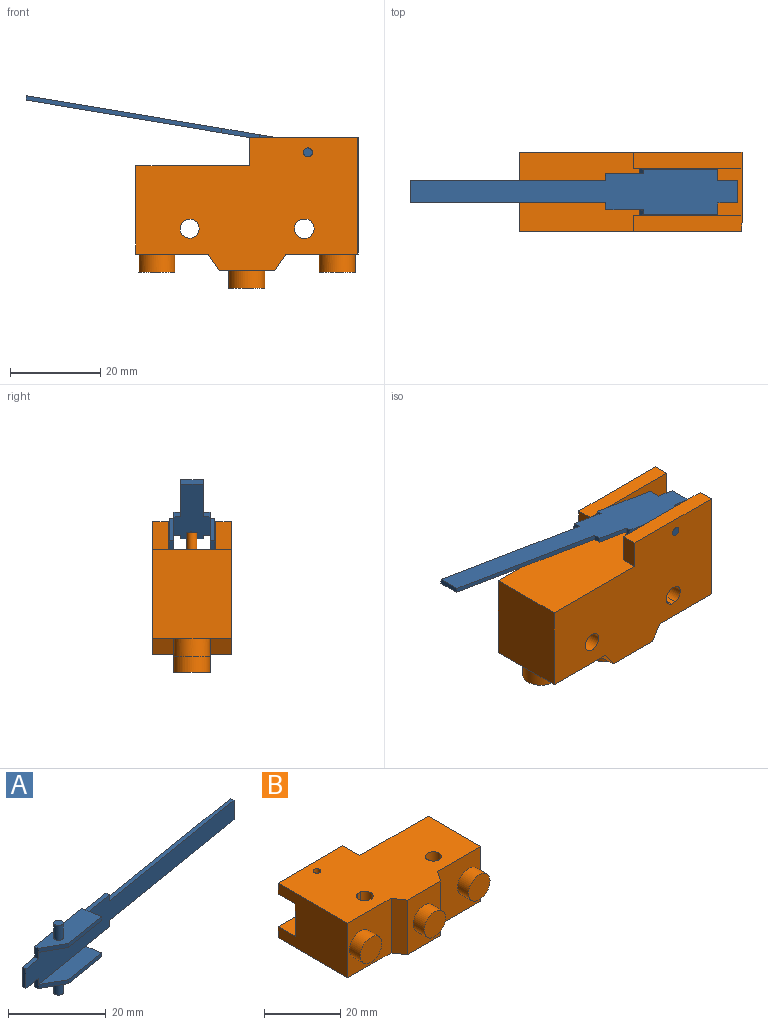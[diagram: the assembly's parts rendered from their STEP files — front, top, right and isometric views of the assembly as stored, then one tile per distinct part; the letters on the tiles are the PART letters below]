
ASSEMBLY  parts=2 mates=1
PART A: 28 faces, bbox 72.6x15.5x17.5 mm
  f0: plane 17.11x5.88mm, normal (0,0,1), area 56.7mm2, adj f1,f2,f3,f4
  f1: plane 11.52x1.93mm, normal (0.17,-0.99,0), area 11.7mm2, adj f0,f2,f3,f5
  f2: plane 5.59x3.12mm, normal (-0.49,-0.87,0), area 6.4mm2, adj f0,f1,f5,f6
  f3: plane 4.93x1.05mm, normal (0.99,0.17,0), area 5.1mm2, adj f0,f1,f4,f5,f7,f8
  f4: plane 72.42x12.14mm, normal (0.17,-0.99,0), area 439.5mm2, adj f0,f3,f6,f7,f9,f10,f11,f12
  f5: plane 17.28x6.86mm, normal (0,0,-1), area 70.3mm2, adj f1,f2,f3,f6,f8,f21
  f6: plane 2.6x0.99mm, normal (-0.99,-0.17,0), area 2.6mm2, adj f2,f4,f5,f8,f9
  f7: plane 8.55x2.39mm, normal (0,0,-1), area 8.5mm2, adj f3,f4,f8,f14
  f8: plane 72.42x12.14mm, normal (-0.17,0.99,0), area 472.9mm2, adj f3,f5,f6,f7,f9,f10,f12,f13
  f9: plane 4.53x1.72mm, normal (0,0,-1), area 4.4mm2, adj f4,f6,f8,f20
  f10: plane 4.93x1.05mm, normal (0.99,0.17,0), area 5.1mm2, adj f4,f8,f11,f12,f22,f23
  f11: plane 17.11x5.88mm, normal (0,0,-1), area 56.7mm2, adj f4,f10,f23,f24
  f12: plane 8.55x2.39mm, normal (0,0,1), area 8.5mm2, adj f4,f8,f10,f16
  f13: plane 43.38x8.23mm, normal (0,0,-1), area 43.8mm2, adj f4,f8,f14,f17
  f14: plane 1.55x0.99mm, normal (0.99,0.17,0), area 1.6mm2, adj f4,f7,f8,f13
  f15: plane 4.53x1.72mm, normal (0,0,1), area 4.4mm2, adj f4,f8,f18,f20
  f16: plane 1.55x0.99mm, normal (0.99,0.17,0), area 1.6mm2, adj f4,f8,f12,f19
  f17: plane 4.9x0.99mm, normal (0.99,0.17,0), area 4.9mm2, adj f4,f8,f13,f19
  f18: plane 2.6x0.99mm, normal (-0.99,-0.17,0), area 2.6mm2, adj f4,f8,f15,f22,f24
  f19: plane 43.38x8.23mm, normal (0,0,1), area 43.8mm2, adj f4,f8,f16,f17
  f20: plane 4.9x0.99mm, normal (-0.99,-0.17,0), area 4.9mm2, adj f4,f8,f9,f15
  f21: cylinder r=1mm len=3.68mm, axis (0,0,-1), area 23.1mm2, adj f5,f25
  f22: plane 17.28x6.86mm, normal (0,0,1), area 70.3mm2, adj f8,f10,f18,f23,f24,f26
  f23: plane 11.52x1.93mm, normal (0.17,-0.99,0), area 11.7mm2, adj f10,f11,f22,f24
  f24: plane 5.59x3.12mm, normal (-0.49,-0.87,0), area 6.4mm2, adj f11,f18,f22,f23
  f25: plane 2x2mm, normal (0,0,-1), area 3.1mm2, adj f21
  f26: cylinder r=1mm len=3.68mm, axis (0,0,-1), area 23.1mm2, adj f22,f27
  f27: plane 2x2mm, normal (0,0,1), area 3.1mm2, adj f26
PART B: 31 faces, bbox 49.2x33.4x17.5 mm
  f0: plane 24x6.3mm, normal (0,0,-1), area 148.1mm2, adj f1,f2,f3,f4,f5
  f1: plane 49.2x17.45mm, normal (0,1,0), area 686.4mm2, adj f0,f2,f3,f6,f7,f8,f9,f10
  f2: plane 6.3x3.5mm, normal (1,0,0), area 22.1mm2, adj f0,f1,f4,f11
  f3: plane 25.8x17.45mm, normal (-1,0,0), area 384.4mm2, adj f0,f1,f4,f7,f9,f11,f12,f13
  f4: plane 24x3.5mm, normal (0,1,0), area 84mm2, adj f0,f2,f3,f11
  f5: cylinder r=1mm len=3.5mm, axis (0,0,-1), area 22mm2, adj f0,f11
  f6: plane 19.5x17.45mm, normal (1,0,0), area 340.3mm2, adj f1,f7,f11,f14
  f7: plane 49.2x29.4mm, normal (0,0,-1), area 1131.9mm2, adj f1,f3,f6,f10,f12,f13,f14,f15
  f8: cylinder r=1.15mm len=3.79mm, axis (0,1,0), area 27.4mm2, adj f1,f24
  f9: plane 24x6.3mm, normal (0,0,1), area 148.1mm2, adj f1,f3,f10,f13,f15
  f10: plane 6.3x3.5mm, normal (1,0,0), area 22.1mm2, adj f1,f7,f9,f13
  f11: plane 49.2x29.4mm, normal (0,0,1), area 1131.9mm2, adj f1,f2,f3,f4,f5,f6,f12,f14
  f12: plane 17.45x16mm, normal (0,-1,0), area 228.9mm2, adj f3,f7,f11,f17,f25
  f13: plane 24x3.5mm, normal (0,1,0), area 84mm2, adj f3,f7,f9,f10
  f14: plane 17.45x16mm, normal (0,-1,0), area 228.9mm2, adj f6,f7,f11,f20,f26
  f15: cylinder r=1mm len=3.5mm, axis (0,0,-1), area 22mm2, adj f7,f9
  f16: plane 17.45x1.17mm, normal (0,-1,0), area 20.4mm2, adj f7,f11,f19,f23
  f17: plane 17.45x3.6mm, normal (-0.83,-0.56,0), area 76mm2, adj f7,f11,f12,f22
  f18: cylinder r=2.1mm len=17.45mm, axis (0,0,-1), area 230.2mm2, adj f7,f11
  f19: cylinder r=2.18mm len=17.45mm, axis (0,0,-1), area 98.8mm2, adj f7,f11,f16,f21
  f20: plane 17.45x3.6mm, normal (0.83,-0.56,0), area 76mm2, adj f7,f11,f14,f22
  f21: plane 17.45x1.17mm, normal (0,1,0), area 20.4mm2, adj f7,f11,f19,f23
  f22: plane 17.45x12.3mm, normal (0,-1,0), area 164.4mm2, adj f7,f11,f17,f20,f27
  f23: cylinder r=2.18mm len=17.45mm, axis (0,0,-1), area 98.8mm2, adj f7,f11,f16,f21
  f24: sphere r=2.3mm, area 4.5mm2, adj f8
  f25: cylinder r=4mm len=8mm, axis (0,1,0), area 100.5mm2, adj f12,f28
  f26: cylinder r=4mm len=8mm, axis (0,1,0), area 100.5mm2, adj f14,f29
  f27: cylinder r=4mm len=8mm, axis (0,1,0), area 100.5mm2, adj f22,f30
  f28: plane 8x8mm, normal (0,-1,0), area 50.3mm2, adj f25
  f29: plane 8x8mm, normal (0,-1,0), area 50.3mm2, adj f26
  f30: plane 8x8mm, normal (0,-1,0), area 50.3mm2, adj f27
PLACE A rot(axis=(0,0.71,0.71),180deg) t=(22.74,-17.52,17.96)mm
PLACE B rot(axis=(0,0.71,0.71),180deg) t=(-3.46,-17.52,1.06)mm
MATE revolute A.f21 <-> B.f5  axis (0,-1,0) through (22.74,-26.25,17.96)mm
